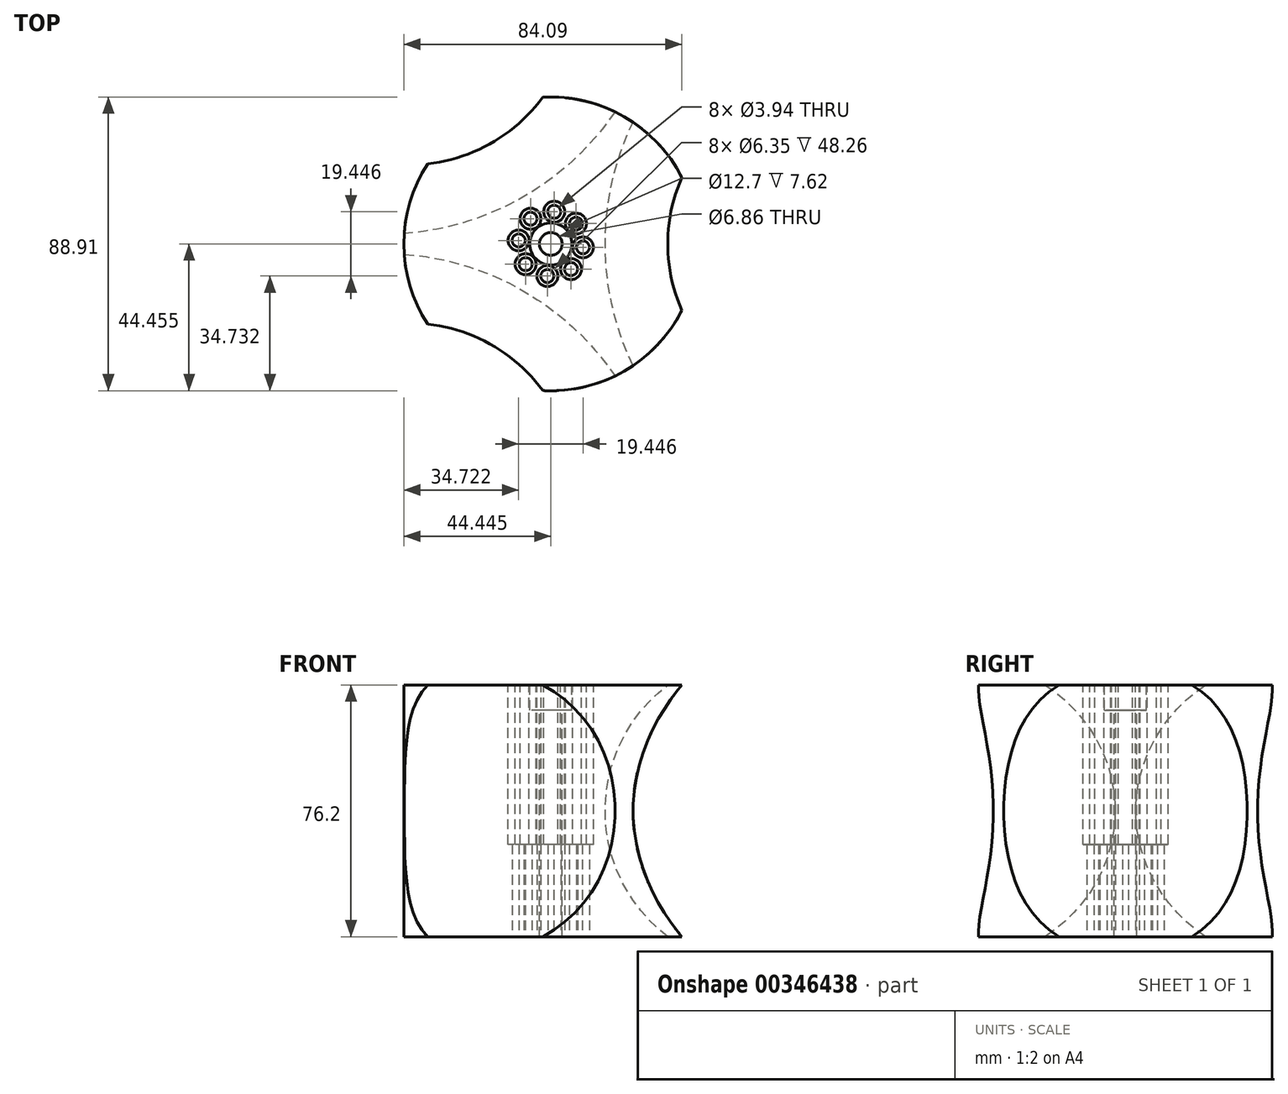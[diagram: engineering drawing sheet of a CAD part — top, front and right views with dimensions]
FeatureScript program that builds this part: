
annotation { "Feature Type Name" : "Feature", "Feature Type Description" : "" }
export const myFeature = defineFeature(function(context is Context, id is Id, definition is map)
    precondition{}
    {
        {
            var Q0;
            Q0=qCreatedBy(makeId("Top.planeOp"),FACE);
            var sketch = newSketch(context, id + "F0", { "sketchPlane" : qUnion([Q0])});
            skCircle(sketch, "E0", {"center": v(-96.8, 47.63) * mm, "radius": 44.45 * mm});
            skCircle(sketch, "E1", {"center": v(-96.8, 47.63) * mm, "radius": 16.51 * mm});
            skCircle(sketch, "E2", {"center": v(-96.8, 47.63) * mm, "radius": 9.78 * mm});
            skCircle(sketch, "E3", {"center": v(-89.18, 53.76) * mm, "radius": 1.97 * mm});
            skCircle(sketch, "E4.1.0", {"center": v(-95.75, 57.35) * mm, "radius": 1.97 * mm});
            skCircle(sketch, "E4.2.0", {"center": v(-102.93, 55.24) * mm, "radius": 1.97 * mm});
            skCircle(sketch, "E4.3.0", {"center": v(-106.52, 48.67) * mm, "radius": 1.97 * mm});
            skCircle(sketch, "E4.4.0", {"center": v(-104.41, 41.5) * mm, "radius": 1.97 * mm});
            skCircle(sketch, "E4.5.0", {"center": v(-97.84, 37.9) * mm, "radius": 1.97 * mm});
            skCircle(sketch, "E4.6.0", {"center": v(-90.66, 40) * mm, "radius": 1.97 * mm});
            skCircle(sketch, "E4.7.0", {"center": v(-87.07, 46.58) * mm, "radius": 1.97 * mm});
            skSolve(sketch);
        }
        {
            var Q0;
            Q0=makeQuery(id+"F0.imprint","IMPRINT",FACE,{"disambiguationData":[TD([[makeQuery(id+"F0.imprint","IMPRINT",EDGE,{"derivedFrom":sQuery(id+"F0.wireOp",EDGE,"E0")}),1.0]])]});
            var Q1;
            Q1=makeQuery(id+"F0.imprint","IMPRINT",FACE,{"disambiguationData":[TD([[makeQuery(id+"F0.imprint","IMPRINT",EDGE,{"derivedFrom":sQuery(id+"F0.wireOp",EDGE,"E1")}),1.0]])]});
            var Q2;
            {var subQ1=sQuery(id+"F0.wireOp",EDGE,"E2");var subQ4=sQuery(id+"F0.wireOp",EDGE,"E3");var subQ5=makeQuery(id+"F0.imprint","INTERSECT",VERTEX,{"disambiguationData":[OD(0.0)],"derivedFrom":[subQ1,subQ4]});Q2=makeQuery(id+"F0.imprint","IMPRINT",FACE,{"disambiguationData":[TD([[makeQuery(id+"F0.imprint","IMPRINT",EDGE,{"disambiguationData":[TD([[subQ5,1.0]])],"derivedFrom":subQ1}),1.0]])]});}
            extrude(context, id + "F1", {"entities" : qUnion([Q0, Q1, Q2]), "depth" : 38.1 * mm, "hasSecondDirection" : true, "secondDirectionOppositeDirection" : true, "secondDirectionDepth" : 38.1 * mm});
        }
        {
            var Q0;
            Q0=qCreatedBy(makeId("Top.planeOp"),FACE);
            var sketch = newSketch(context, id + "F2", { "sketchPlane" : qUnion([Q0])});
            skCircle(sketch, "E5.0.0", {"center": v(-96.8, 47.63) * mm, "radius": 44.45 * mm});
            skCircle(sketch, "E6", {"center": v(-96.8, 47.63) * mm, "radius": 16.51 * mm});
            skLineSegment(sketch, "E7", {"start": v(-32.58, 47.63) * mm, "end": v(-32.58, 89.03) * mm});
            skLineSegment(sketch, "E8", {"start": v(-32.58, -6.48) * mm, "end": v(-32.58, 89.03) * mm});
            skLineSegment(sketch, "E9", {"start": v(-32.58, 47.63) * mm, "end": v(-32.58, -28.57) * mm});
            skLineSegment(sketch, "E10", {"start": v(-32.58, 47.63) * mm, "end": v(-32.58, 123.82) * mm});
            skPoint(sketch, "E11", {"position": v(-80.34, 45.07) * mm});
            skArc(sketch, "E12", {"start": v(-32.58, -28.57) * mm, "mid": v(15.17, 47.63) * mm, "end": v(-32.58, 123.83) * mm});
            skPoint(sketch, "E13", {"position": v(15.17, 47.63) * mm});
            skLineSegment(sketch, "E14.1.0", {"start": v(-128.9, 103.23) * mm, "end": v(-62.9, 141.33) * mm});
            skPoint(sketch, "E14.1.1", {"position": v(-152.78, 144.59) * mm});
            skArc(sketch, "E14.1.2", {"start": v(-62.9, 141.33) * mm, "mid": v(-152.78, 144.59) * mm, "end": v(-194.9, 65.13) * mm});
            skLineSegment(sketch, "E14.1.3", {"start": v(-128.9, 103.23) * mm, "end": v(-194.9, 65.13) * mm});
            skLineSegment(sketch, "E14.1.4", {"start": v(-82.05, 130.28) * mm, "end": v(-164.76, 82.53) * mm});
            skLineSegment(sketch, "E14.1.5", {"start": v(-128.9, 103.23) * mm, "end": v(-164.76, 82.53) * mm});
            skLineSegment(sketch, "E14.2.0", {"start": v(-128.9, -7.98) * mm, "end": v(-194.9, 30.12) * mm});
            skPoint(sketch, "E14.2.1", {"position": v(-152.78, -49.34) * mm});
            skArc(sketch, "E14.2.2", {"start": v(-194.9, 30.12) * mm, "mid": v(-152.78, -49.34) * mm, "end": v(-62.9, -46.08) * mm});
            skLineSegment(sketch, "E14.2.3", {"start": v(-128.9, -7.98) * mm, "end": v(-62.9, -46.08) * mm});
            skLineSegment(sketch, "E14.2.4", {"start": v(-175.75, 19.07) * mm, "end": v(-93.05, -28.68) * mm});
            skLineSegment(sketch, "E14.2.5", {"start": v(-128.9, -7.98) * mm, "end": v(-93.05, -28.68) * mm});
            skLineSegment(sketch, "E15", {"start": v(-96.8, 47.63) * mm, "end": v(-27.32, 47.63) * mm});
            skLineSegment(sketch, "E16", {"start": v(-96.8, 47.63) * mm, "end": v(-142.85, 127.4) * mm});
            skLineSegment(sketch, "E17", {"start": v(-96.8, 47.63) * mm, "end": v(-144.07, -34.25) * mm});
            skSolve(sketch);
        }
        {
            var Q0;
            Q0=makeQuery(id+"F2.imprint","IMPRINT",FACE,{"disambiguationData":[TD([[makeQuery(id+"F2.imprint","IMPRINT",EDGE,{"derivedFrom":sQuery(id+"F2.wireOp",EDGE,"E14.2.0")}),1.0]])]});
            var Q1;
            Q1=makeQuery(id+"F2.imprint","IMPRINT",FACE,{"disambiguationData":[TD([[makeQuery(id+"F2.imprint","IMPRINT",EDGE,{"derivedFrom":sQuery(id+"F2.wireOp",EDGE,"E14.1.0")}),1.0]])]});
            var Q2;
            {var subQ0=sQuery(id+"F2.wireOp",EDGE,"E12");Q2=makeQuery(id+"F2.imprint","IMPRINT",FACE,{"disambiguationData":[TD([[makeQuery(id+"F2.imprint","IMPRINT",EDGE,{"derivedFrom":subQ0}),1.0]])]});}
            var Q3;
            Q3=sQuery(id+"F2.wireOp",EDGE,"aOpEJ7Df-Mzx5-U4IW-AKo9-5E0Zru6Bx9m7");
            var Q4;
            Q4=sQuery(id+"F2.wireOp",EDGE,"E14.2.4");
            revolve(context, id + "F3", {"operationType" : NewBodyOperationType.REMOVE, "entities" : qUnion([Q0, Q1, Q2]), "surfaceEntities" : qUnion([Q3]), "axis" : qUnion([Q4]), "revolveType" : RevolveType.FULL, "oppositeDirection" : true});
        }
        {
            var Q0;
            Q0=makeQuery(id+"F1.opExtrude","CAP_FACE",FACE,{"disambiguationData":[OSD([sQuery(id+"F0.wireOp",EDGE,"E0"),sQuery(id+"F0.wireOp",EDGE,"E3"),sQuery(id+"F0.wireOp",EDGE,"E4.1.0"),sQuery(id+"F0.wireOp",EDGE,"E4.2.0"),sQuery(id+"F0.wireOp",EDGE,"E4.3.0"),sQuery(id+"F0.wireOp",EDGE,"E4.4.0"),sQuery(id+"F0.wireOp",EDGE,"E4.5.0"),sQuery(id+"F0.wireOp",EDGE,"E4.6.0"),sQuery(id+"F0.wireOp",EDGE,"E4.7.0")])],"isStart":false});
            var sketch = newSketch(context, id + "F4", { "sketchPlane" : qUnion([Q0])});
            skCircle(sketch, "E18.0", {"center": v(-102.93, 55.24) * mm, "radius": 1.97 * mm});
            skCircle(sketch, "E19", {"center": v(-102.93, 55.24) * mm, "radius": 3.18 * mm});
            skCircle(sketch, "E20.1.0", {"center": v(-95.75, 57.35) * mm, "radius": 3.18 * mm});
            skCircle(sketch, "E20.2.0", {"center": v(-89.18, 53.76) * mm, "radius": 3.18 * mm});
            skCircle(sketch, "E20.3.0", {"center": v(-87.07, 46.58) * mm, "radius": 3.18 * mm});
            skCircle(sketch, "E20.4.0", {"center": v(-90.66, 40) * mm, "radius": 3.18 * mm});
            skCircle(sketch, "E20.5.0", {"center": v(-97.84, 37.9) * mm, "radius": 3.18 * mm});
            skCircle(sketch, "E20.6.0", {"center": v(-104.41, 41.5) * mm, "radius": 3.18 * mm});
            skCircle(sketch, "E20.7.0", {"center": v(-106.52, 48.67) * mm, "radius": 3.18 * mm});
            skPoint(sketch, "E20.center", {"position": v(-96.8, 47.63) * mm});
            skLineSegment(sketch, "E20.anchor1", {"start": v(-96.8, 47.63) * mm, "end": v(-102.93, 55.24) * mm, "construction": true});
            skLineSegment(sketch, "E20.anchor2", {"start": v(-96.8, 47.63) * mm, "end": v(-106.52, 48.67) * mm, "construction": true});
            skSolve(sketch);
        }
        {
            var Q0;
            Q0=makeQuery(id+"F4.imprint","IMPRINT",FACE,{"disambiguationData":[TD([[makeQuery(id+"F4.imprint","IMPRINT",EDGE,{"derivedFrom":sQuery(id+"F4.wireOp",EDGE,"E18.0")}),-1.0]])]});
            var Q1;
            Q1=makeQuery(id+"F4.imprint","IMPRINT",FACE,{"disambiguationData":[TD([[makeQuery(id+"F4.imprint","IMPRINT",EDGE,{"derivedFrom":sQuery(id+"F4.wireOp",EDGE,"E20.1.0")}),1.0]])]});
            var Q2;
            Q2=makeQuery(id+"F4.imprint","IMPRINT",FACE,{"disambiguationData":[TD([[makeQuery(id+"F4.imprint","IMPRINT",EDGE,{"derivedFrom":sQuery(id+"F4.wireOp",EDGE,"E20.2.0")}),1.0]])]});
            var Q3;
            Q3=makeQuery(id+"F4.imprint","IMPRINT",FACE,{"disambiguationData":[TD([[makeQuery(id+"F4.imprint","IMPRINT",EDGE,{"derivedFrom":sQuery(id+"F4.wireOp",EDGE,"E20.3.0")}),1.0]])]});
            var Q4;
            Q4=makeQuery(id+"F4.imprint","IMPRINT",FACE,{"disambiguationData":[TD([[makeQuery(id+"F4.imprint","IMPRINT",EDGE,{"derivedFrom":sQuery(id+"F4.wireOp",EDGE,"E20.4.0")}),1.0]])]});
            var Q5;
            Q5=makeQuery(id+"F4.imprint","IMPRINT",FACE,{"disambiguationData":[TD([[makeQuery(id+"F4.imprint","IMPRINT",EDGE,{"derivedFrom":sQuery(id+"F4.wireOp",EDGE,"E20.5.0")}),1.0]])]});
            var Q6;
            Q6=makeQuery(id+"F4.imprint","IMPRINT",FACE,{"disambiguationData":[TD([[makeQuery(id+"F4.imprint","IMPRINT",EDGE,{"derivedFrom":sQuery(id+"F4.wireOp",EDGE,"E20.6.0")}),1.0]])]});
            var Q7;
            Q7=makeQuery(id+"F4.imprint","IMPRINT",FACE,{"disambiguationData":[TD([[makeQuery(id+"F4.imprint","IMPRINT",EDGE,{"derivedFrom":sQuery(id+"F4.wireOp",EDGE,"E20.7.0")}),1.0]])]});
            var Q8;
            Q8=sQuery(id+"F4.wireOp",EDGE,"E19");
            var Q9;
            Q9=sQuery(id+"F4.wireOp",EDGE,"E20.1.0");
            var Q10;
            Q10=sQuery(id+"F4.wireOp",EDGE,"E20.2.0");
            var Q11;
            Q11=sQuery(id+"F4.wireOp",EDGE,"E20.3.0");
            var Q12;
            Q12=sQuery(id+"F4.wireOp",EDGE,"E20.4.0");
            var Q13;
            Q13=sQuery(id+"F4.wireOp",EDGE,"E20.5.0");
            var Q14;
            Q14=sQuery(id+"F4.wireOp",EDGE,"E20.6.0");
            var Q15;
            Q15=sQuery(id+"F4.wireOp",EDGE,"E20.7.0");
            extrude(context, id + "F5", {"entities" : qUnion([Q0, Q1, Q2, Q3, Q4, Q5, Q6, Q7]), "operationType" : NewBodyOperationType.REMOVE, "surfaceEntities" : qUnion([Q8, Q9, Q10, Q11, Q12, Q13, Q14, Q15]), "oppositeDirection" : true, "depth" : 48.26 * mm});
        }
        {
            var Q0;
            Q0=makeQuery(id+"F1.opExtrude","CAP_FACE",FACE,{"disambiguationData":[OSD([sQuery(id+"F0.wireOp",EDGE,"E0"),sQuery(id+"F0.wireOp",EDGE,"E3"),sQuery(id+"F0.wireOp",EDGE,"E4.1.0"),sQuery(id+"F0.wireOp",EDGE,"E4.2.0"),sQuery(id+"F0.wireOp",EDGE,"E4.3.0"),sQuery(id+"F0.wireOp",EDGE,"E4.4.0"),sQuery(id+"F0.wireOp",EDGE,"E4.5.0"),sQuery(id+"F0.wireOp",EDGE,"E4.6.0"),sQuery(id+"F0.wireOp",EDGE,"E4.7.0")])],"isStart":false});
            var sketch = newSketch(context, id + "F6", { "sketchPlane" : qUnion([Q0])});
            skCircle(sketch, "E21", {"center": v(-96.8, 47.63) * mm, "radius": 6.35 * mm});
            skSolve(sketch);
        }
        {
            var Q0;
            Q0=qSketchRegion(id+"F6",true);
            extrude(context, id + "F7", {"entities" : qUnion([Q0]), "operationType" : NewBodyOperationType.REMOVE, "oppositeDirection" : true, "depth" : 7.62 * mm});
        }
        {
            var Q0;
            Q0=makeQuery(id+"F7.boolean.opBoolean","COPY",FACE,{"derivedFrom":makeQuery(id+"F7.opExtrude","CAP_FACE",FACE,{"disambiguationData":[OSD([sQuery(id+"F6.wireOp",EDGE,"E21")])],"isStart":false})});
            var sketch = newSketch(context, id + "F8", { "sketchPlane" : qUnion([Q0])});
            skCircle(sketch, "E22", {"center": v(-96.8, 47.63) * mm, "radius": 3.43 * mm});
            skSolve(sketch);
        }
        {
            var Q0;
            Q0=makeQuery(id+"F8.imprint","IMPRINT",FACE,{"disambiguationData":[TD([[makeQuery(id+"F8.imprint","IMPRINT",EDGE,{"derivedFrom":sQuery(id+"F8.wireOp",EDGE,"E22")}),1.0]])]});
            extrude(context, id + "F9", {"entities" : qUnion([Q0]), "operationType" : NewBodyOperationType.REMOVE, "endBound" : BoundingType.UP_TO_NEXT, "oppositeDirection" : true, "depth" : 25.4 * mm});
        }
        {
            var Q0;
            {var subQ0=sQuery(id+"F2.wireOp",EDGE,"E12");Q0=makeQuery(id+"F2.imprint","IMPRINT",FACE,{"disambiguationData":[TD([[makeQuery(id+"F2.imprint","IMPRINT",EDGE,{"derivedFrom":subQ0}),1.0]])]});}
            var Q1;
            Q1=sQuery(id+"F2.wireOp",EDGE,"E10");
            revolve(context, id + "F10", {"operationType" : NewBodyOperationType.REMOVE, "entities" : qUnion([Q0]), "axis" : qUnion([Q1]), "revolveType" : RevolveType.FULL, "oppositeDirection" : true});
        }
        {
            var Q0;
            Q0=makeQuery(id+"F2.imprint","IMPRINT",FACE,{"disambiguationData":[TD([[makeQuery(id+"F2.imprint","IMPRINT",EDGE,{"derivedFrom":sQuery(id+"F2.wireOp",EDGE,"E14.1.0")}),1.0]])]});
            var Q1;
            Q1=sQuery(id+"F2.wireOp",EDGE,"E14.1.4");
            revolve(context, id + "F11", {"operationType" : NewBodyOperationType.REMOVE, "entities" : qUnion([Q0]), "axis" : qUnion([Q1]), "revolveType" : RevolveType.FULL, "oppositeDirection" : true});
        }
    });
